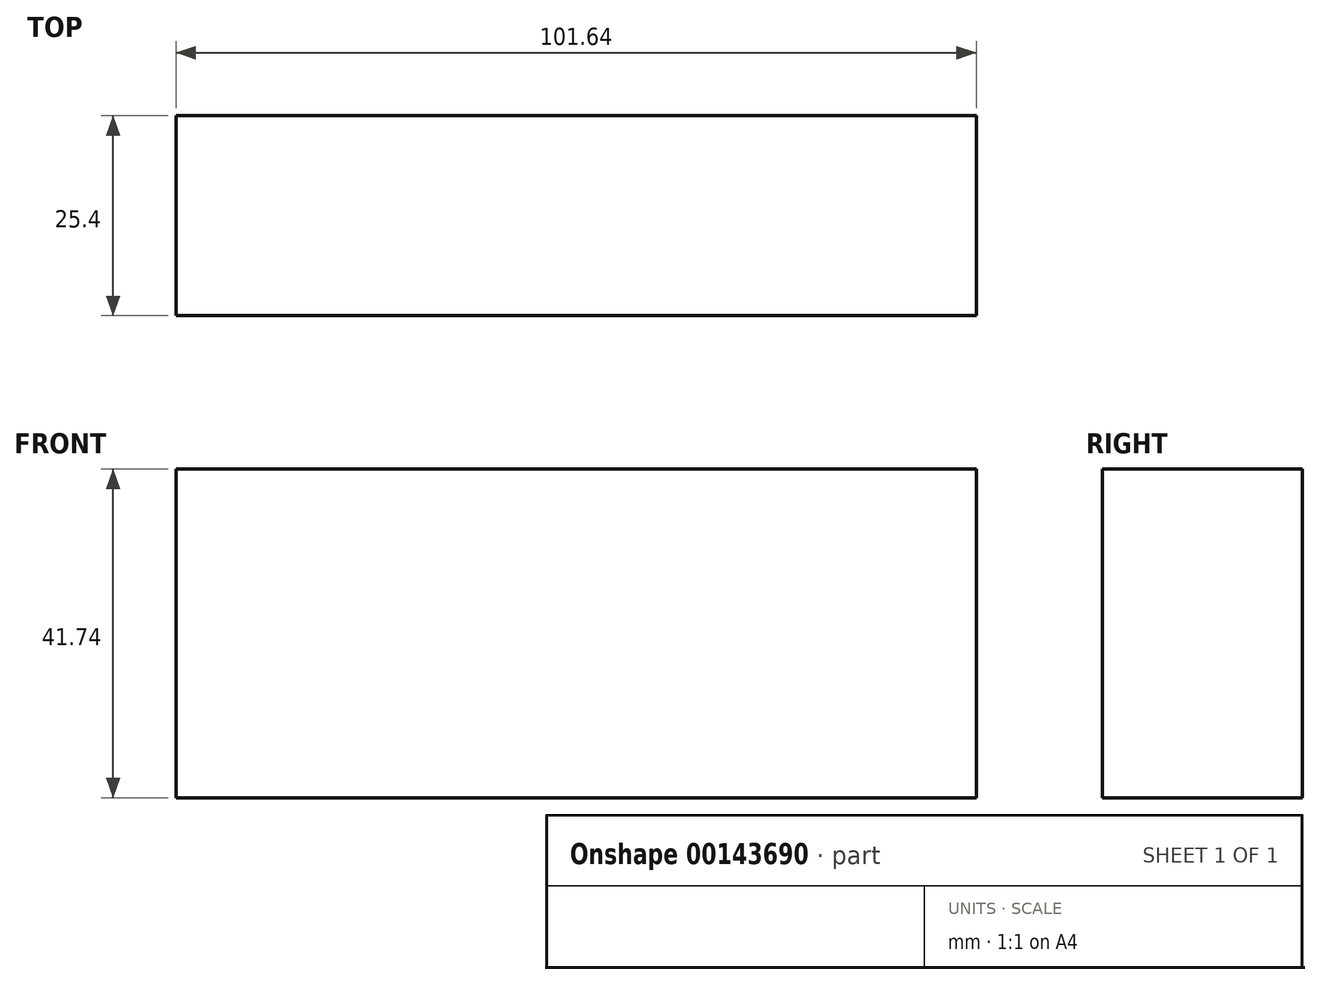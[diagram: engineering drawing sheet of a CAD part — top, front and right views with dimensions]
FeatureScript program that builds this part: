
annotation { "Feature Type Name" : "Feature", "Feature Type Description" : "" }
export const myFeature = defineFeature(function(context is Context, id is Id, definition is map)
    precondition{}
    {
        {
            var Q0;
            Q0=qCreatedBy(makeId("Front.planeOp"),FACE);
            var sketch = newSketch(context, id + "F0", { "sketchPlane" : qUnion([Q0])});
            skLineSegment(sketch, "E0.bottom", {"start": v(-50.82, 20.87) * mm, "end": v(50.82, 20.87) * mm});
            skLineSegment(sketch, "E0.top", {"start": v(-50.82, -20.87) * mm, "end": v(50.82, -20.87) * mm});
            skLineSegment(sketch, "E0.left", {"start": v(-50.82, 20.87) * mm, "end": v(-50.82, -20.87) * mm});
            skLineSegment(sketch, "E0.right", {"start": v(50.82, 20.87) * mm, "end": v(50.82, -20.87) * mm});
            skPoint(sketch, "E0.middle", {"position": v(0, 0) * mm});
            skSolve(sketch);
        }
        {
            var Q0;
            Q0 = qSketchRegion(id + "F0", true);
            extrude(context, id + "F1", {"entities" : qUnion([Q0]), "endBound" : BoundingType.SYMMETRIC, "depth" : 25.4 * mm});
        }
    });
